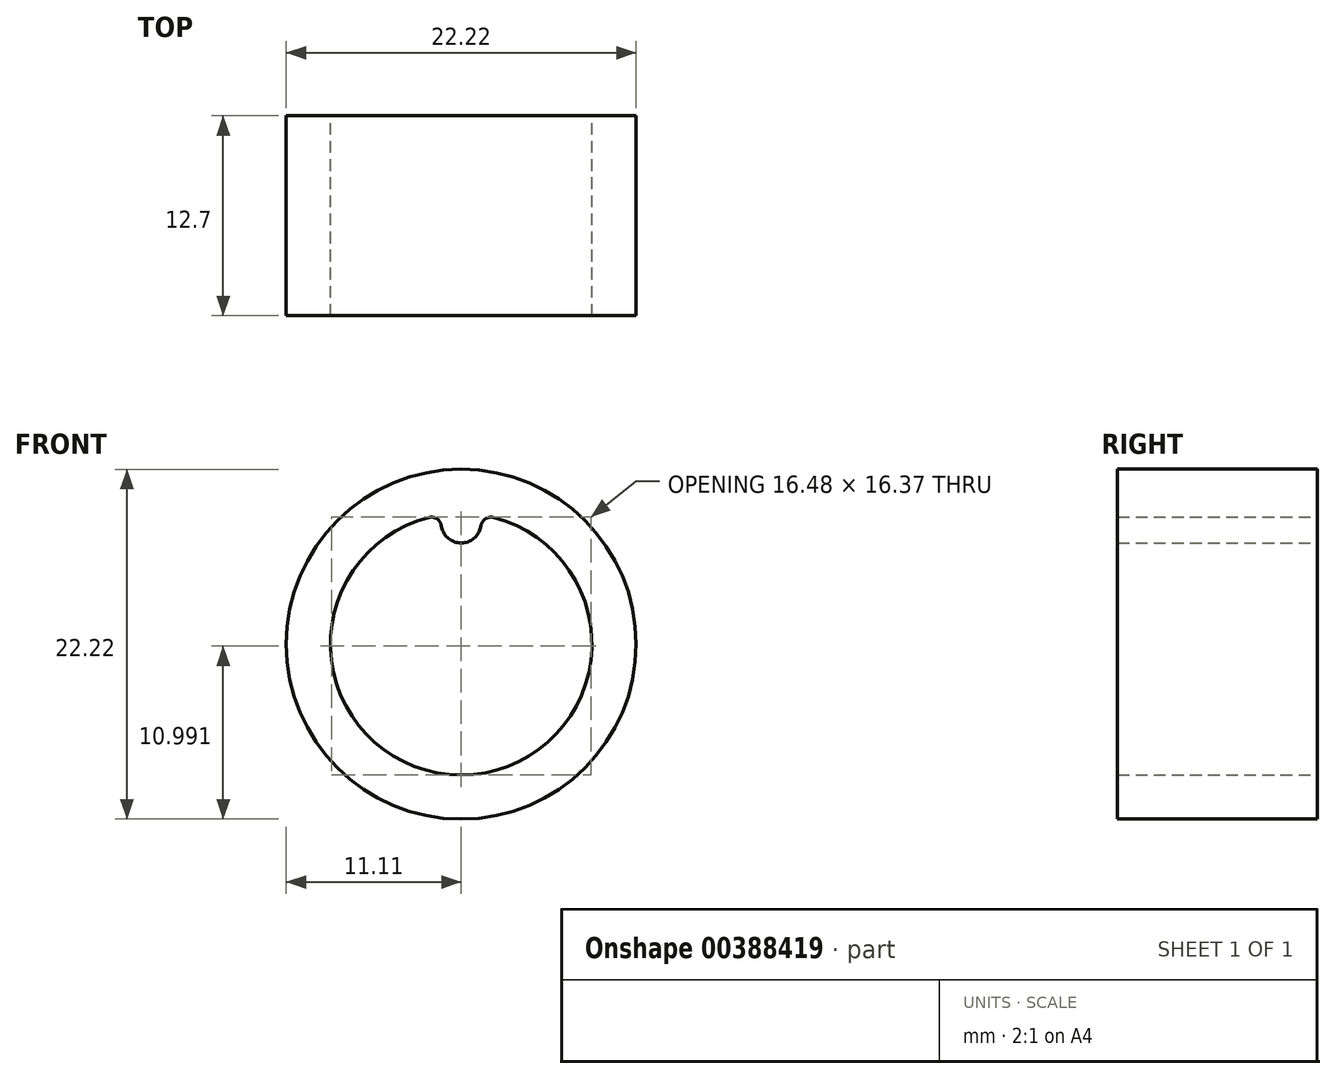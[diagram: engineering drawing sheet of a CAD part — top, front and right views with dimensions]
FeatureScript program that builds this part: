
annotation { "Feature Type Name" : "Feature", "Feature Type Description" : "" }
export const myFeature = defineFeature(function(context is Context, id is Id, definition is map)
    precondition{}
    {
        {
            var Q0;
            Q0=qCreatedBy(makeId("Front.planeOp"),FACE);
            var sketch = newSketch(context, id + "F0", { "sketchPlane" : qUnion([Q0])});
            skCircle(sketch, "E0", {"center": v(0, 0) * mm, "radius": 6.4 * mm});
            skSolve(sketch);
        }
        {
            var Q0;
            Q0=qCreatedBy(makeId("Front.planeOp"),FACE);
            var sketch = newSketch(context, id + "F1", { "sketchPlane" : qUnion([Q0])});
            skCircle(sketch, "E1", {"center": v(0, 0) * mm, "radius": 11.11 * mm});
            skCircle(sketch, "E2", {"center": v(0, 0) * mm, "radius": 8.3 * mm});
            skSolve(sketch);
        }
        {
            var Q0;
            Q0 = qSketchRegion(id + "F1", true);
            extrude(context, id + "F2", {"entities" : qUnion([Q0]), "depth" : 12.7 * mm});
        }
        {
            var Q0;
            Q0=makeQuery(id+"F2.opExtrude","CAP_FACE",FACE,{"disambiguationData":[OSD([sQuery(id+"F1.wireOp",EDGE,"E1"),sQuery(id+"F1.wireOp",EDGE,"E2")])],"isStart":true});
            var sketch = newSketch(context, id + "F3", { "sketchPlane" : qUnion([Q0])});
            skCircle(sketch, "E3.0", {"center": v(0, 0) * mm, "radius": 6.43 * mm, "construction": true});
            skArc(sketch, "E4", {"start": v(-1.27, 7.57) * mm, "mid": v(-1.56, 7.97) * mm, "end": v(-2.05, 8.05) * mm});
            skArc(sketch, "E5", {"start": v(-1.24, 7.42) * mm, "mid": v(0, 6.43) * mm, "end": v(1.24, 7.42) * mm});
            skArc(sketch, "E6", {"start": v(2.05, 8.05) * mm, "mid": v(1.56, 7.97) * mm, "end": v(1.27, 7.57) * mm});
            skLineSegment(sketch, "E7", {"start": v(1.27, 7.57) * mm, "end": v(1.24, 7.42) * mm});
            skLineSegment(sketch, "E8", {"start": v(-1.24, 7.42) * mm, "end": v(-1.27, 7.57) * mm});
            skArc(sketch, "E9", {"start": v(2.05, 8.05) * mm, "mid": v(0, 8.3) * mm, "end": v(-2.05, 8.05) * mm});
            skSolve(sketch);
        }
        {
            var Q0;
            Q0 = qSketchRegion(id + "F3", true);
            var Q1;
            Q1=makeQuery(id+"F2.opExtrude","CAP_FACE",FACE,{"disambiguationData":[OSD([sQuery(id+"F1.wireOp",EDGE,"E1"),sQuery(id+"F1.wireOp",EDGE,"E2")])],"isStart":false});
            extrude(context, id + "F4", {"entities" : qUnion([Q0]), "operationType" : NewBodyOperationType.ADD, "endBound" : BoundingType.UP_TO_SURFACE, "oppositeDirection" : true, "endBoundEntityFace" : qUnion([Q1]), "depth" : 25.4 * mm});
        }
    });
